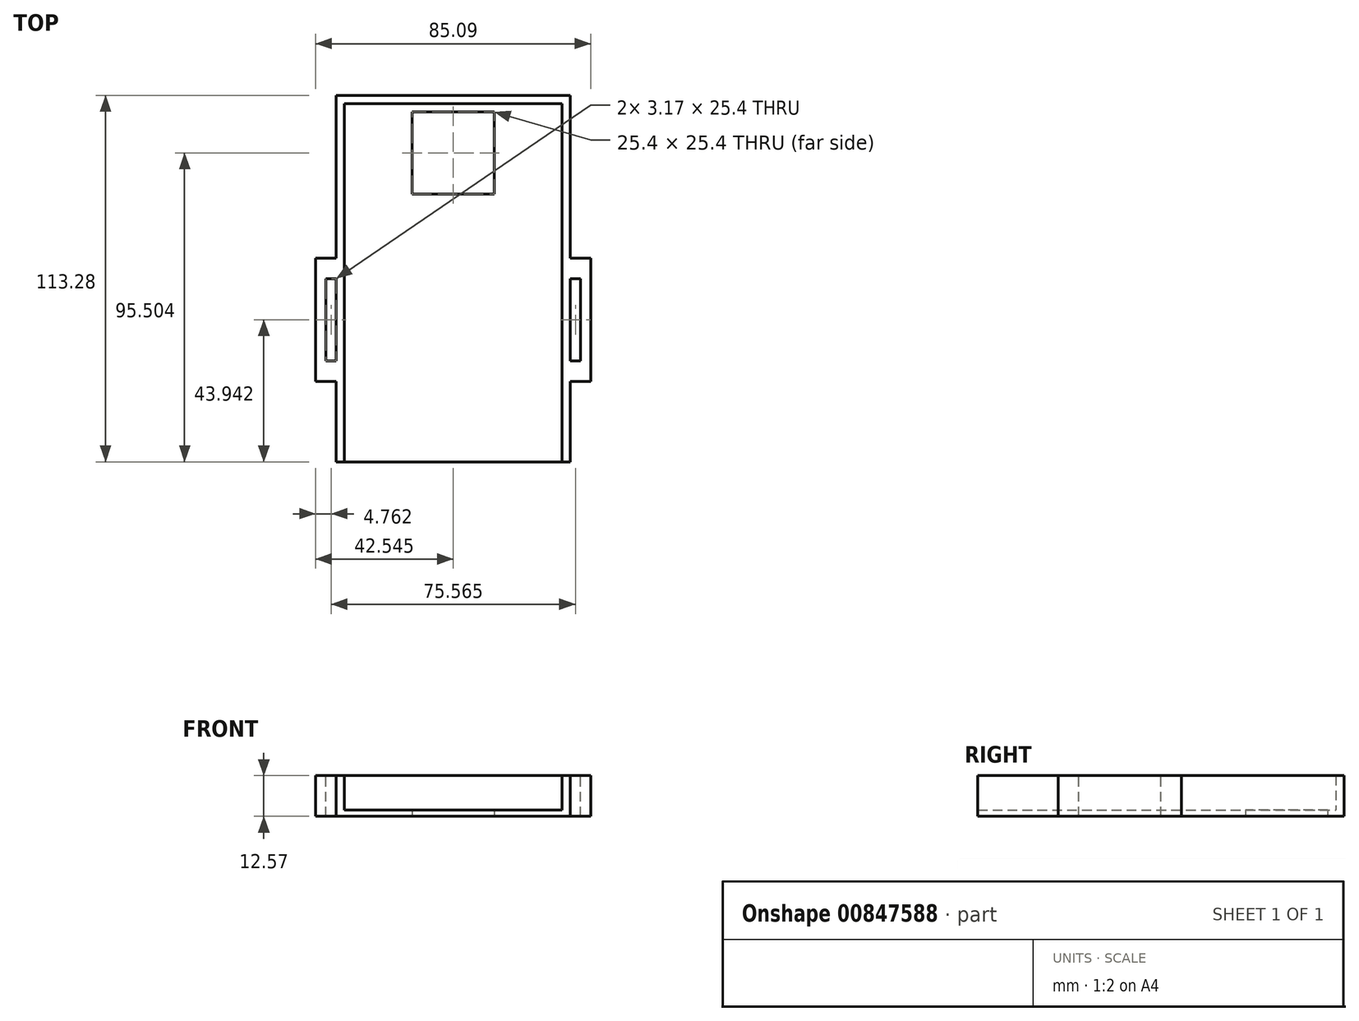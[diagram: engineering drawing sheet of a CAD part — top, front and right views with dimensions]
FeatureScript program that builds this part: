
annotation { "Feature Type Name" : "Feature", "Feature Type Description" : "" }
export const myFeature = defineFeature(function(context is Context, id is Id, definition is map)
    precondition{}
    {
        {
            var Q0;
            Q0=qCreatedBy(makeId("Top.planeOp"),FACE);
            var sketch = newSketch(context, id + "F0", { "sketchPlane" : qUnion([Q0])});
            skLineSegment(sketch, "E0.bottom", {"start": v(0, 0) * mm, "end": v(72.39, 0) * mm});
            skLineSegment(sketch, "E0.top", {"start": v(0, 138.68) * mm, "end": v(72.39, 138.68) * mm});
            skLineSegment(sketch, "E0.left", {"start": v(0, 0) * mm, "end": v(0, 138.68) * mm});
            skLineSegment(sketch, "E0.right", {"start": v(72.39, 0) * mm, "end": v(72.39, 138.68) * mm});
            skSolve(sketch);
        }
        {
            var Q0;
            Q0 = qSketchRegion(id + "F0", true);
            extrude(context, id + "F1", {"entities" : qUnion([Q0]), "depth" : 1.9 * mm, "offsetDistance" : 25.4 * mm});
        }
        {
            var Q0;
            Q0=makeQuery(id+"F1.opExtrude","CAP_FACE",FACE,{"disambiguationData":[OSD([sQuery(id+"F0.wireOp",EDGE,"E0.bottom"),sQuery(id+"F0.wireOp",EDGE,"E0.top"),sQuery(id+"F0.wireOp",EDGE,"E0.left"),sQuery(id+"F0.wireOp",EDGE,"E0.right")])],"isStart":false});
            var sketch = newSketch(context, id + "F2", { "sketchPlane" : qUnion([Q0])});
            skLineSegment(sketch, "E1.bottom", {"start": v(0, 0) * mm, "end": v(72.39, 0) * mm});
            skLineSegment(sketch, "E1.top", {"start": v(0, 138.68) * mm, "end": v(72.39, 138.68) * mm});
            skLineSegment(sketch, "E1.left", {"start": v(0, 0) * mm, "end": v(0, 138.68) * mm});
            skLineSegment(sketch, "E1.right", {"start": v(72.39, 0) * mm, "end": v(72.39, 138.68) * mm});
            skLineSegment(sketch, "E2.bottom", {"start": v(2.54, 2.54) * mm, "end": v(69.85, 2.54) * mm});
            skLineSegment(sketch, "E2.top", {"start": v(2.54, 136.14) * mm, "end": v(69.85, 136.14) * mm});
            skLineSegment(sketch, "E2.left", {"start": v(2.54, 2.54) * mm, "end": v(2.54, 136.14) * mm});
            skLineSegment(sketch, "E2.right", {"start": v(69.85, 2.54) * mm, "end": v(69.85, 136.14) * mm});
            skSolve(sketch);
        }
        {
            var Q0;
            Q0 = qSketchRegion(id + "F2", true);
            extrude(context, id + "F3", {"entities" : qUnion([Q0]), "operationType" : NewBodyOperationType.ADD, "depth" : 10.67 * mm, "offsetDistance" : 25.4 * mm});
        }
        {
            var Q0;
            Q0=makeQuery(id+"F1.opExtrude","CAP_FACE",FACE,{"disambiguationData":[OSD([sQuery(id+"F0.wireOp",EDGE,"E0.bottom"),sQuery(id+"F0.wireOp",EDGE,"E0.top"),sQuery(id+"F0.wireOp",EDGE,"E0.left"),sQuery(id+"F0.wireOp",EDGE,"E0.right")])],"isStart":true});
            var sketch = newSketch(context, id + "F4", { "sketchPlane" : qUnion([Q0])});
            skLineSegment(sketch, "E3.bottom", {"start": v(48.9, -133.6) * mm, "end": v(23.5, -133.6) * mm});
            skLineSegment(sketch, "E3.top", {"start": v(48.9, -108.2) * mm, "end": v(23.5, -108.2) * mm});
            skLineSegment(sketch, "E3.left", {"start": v(48.9, -133.6) * mm, "end": v(48.9, -108.2) * mm});
            skLineSegment(sketch, "E3.right", {"start": v(23.5, -133.6) * mm, "end": v(23.5, -108.2) * mm});
            skSolve(sketch);
        }
        {
            var Q0;
            Q0 = qSketchRegion(id + "F4", true);
            extrude(context, id + "F5", {"entities" : qUnion([Q0]), "operationType" : NewBodyOperationType.REMOVE, "endBound" : BoundingType.UP_TO_NEXT, "oppositeDirection" : true, "depth" : 25.4 * mm, "offsetDistance" : 25.4 * mm});
        }
        {
            var Q0;
            Q0=makeQuery(id+"F3.boolean.opBoolean","MERGE",FACE,{"derivedFrom":[makeQuery(id+"F1.opExtrude","SWEPT_FACE",FACE,{"disambiguationData":[OSD([sQuery(id+"F0.wireOp",EDGE,"E0.right")])]}),makeQuery(id+"F3.opExtrude","SWEPT_FACE",FACE,{"disambiguationData":[OSD([sQuery(id+"F2.wireOp",EDGE,"E1.right")])]})]});
            var sketch = newSketch(context, id + "F6", { "sketchPlane" : qUnion([Q0])});
            skLineSegment(sketch, "E4.left", {"start": v(56.64, 0) * mm, "end": v(56.64, 12.57) * mm});
            skLineSegment(sketch, "E4.right", {"start": v(82.04, 0) * mm, "end": v(82.04, 12.57) * mm});
            skLineSegment(sketch, "E5.bottom", {"start": v(56.64, 12.57) * mm, "end": v(50.3, 12.57) * mm});
            skLineSegment(sketch, "E5.top", {"start": v(56.64, 0) * mm, "end": v(50.3, 0) * mm});
            skLineSegment(sketch, "E5.left", {"start": v(56.64, 12.57) * mm, "end": v(56.64, 0) * mm});
            skLineSegment(sketch, "E5.right", {"start": v(50.3, 12.57) * mm, "end": v(50.3, 0) * mm});
            skLineSegment(sketch, "E6.bottom", {"start": v(82.04, 12.57) * mm, "end": v(88.4, 12.57) * mm});
            skLineSegment(sketch, "E6.top", {"start": v(82.04, 0) * mm, "end": v(88.4, 0) * mm});
            skLineSegment(sketch, "E6.left", {"start": v(82.04, 12.57) * mm, "end": v(82.04, 0) * mm});
            skLineSegment(sketch, "E6.right", {"start": v(88.4, 12.57) * mm, "end": v(88.4, 0) * mm});
            skSolve(sketch);
        }
        {
            var Q0;
            Q0 = qSketchRegion(id + "F6", true);
            extrude(context, id + "F7", {"entities" : qUnion([Q0]), "operationType" : NewBodyOperationType.ADD, "depth" : 3.17 * mm, "offsetDistance" : 25.4 * mm});
        }
        {
            var Q0;
            Q0=makeQuery(id+"F7.opExtrude","SWEPT_FACE",FACE,{"disambiguationData":[OSD([sQuery(id+"F6.wireOp",EDGE,"E5.right")])]});
            var sketch = newSketch(context, id + "F8", { "sketchPlane" : qUnion([Q0])});
            skLineSegment(sketch, "E7.bottom", {"start": v(75.56, 0) * mm, "end": v(78.74, 0) * mm});
            skLineSegment(sketch, "E7.top", {"start": v(75.56, 12.57) * mm, "end": v(78.74, 12.57) * mm});
            skLineSegment(sketch, "E7.left", {"start": v(75.56, 0) * mm, "end": v(75.56, 12.57) * mm});
            skLineSegment(sketch, "E7.right", {"start": v(78.74, 0) * mm, "end": v(78.74, 12.57) * mm});
            skSolve(sketch);
        }
        {
            var Q0;
            Q0 = qSketchRegion(id + "F8", true);
            var Q1;
            Q1=makeQuery(id+"F7.opExtrude","SWEPT_FACE",FACE,{"disambiguationData":[OSD([sQuery(id+"F6.wireOp",EDGE,"E6.right")])]});
            extrude(context, id + "F9", {"entities" : qUnion([Q0]), "operationType" : NewBodyOperationType.ADD, "endBound" : BoundingType.UP_TO_SURFACE, "oppositeDirection" : true, "depth" : 25.4 * mm, "endBoundEntityFace" : qUnion([Q1]), "offsetDistance" : 25.4 * mm});
        }
        {
            var Q0;
            Q0=makeQuery(id+"F9.boolean.opBoolean","MERGE",FACE,{"derivedFrom":[makeQuery(id+"F7.boolean.opBoolean","MERGE",FACE,{"derivedFrom":[makeQuery(id+"F3.opExtrude","CAP_FACE",FACE,{"disambiguationData":[OSD([sQuery(id+"F2.wireOp",EDGE,"E1.bottom"),sQuery(id+"F2.wireOp",EDGE,"E1.top"),sQuery(id+"F2.wireOp",EDGE,"E1.left"),sQuery(id+"F2.wireOp",EDGE,"E1.right"),sQuery(id+"F2.wireOp",EDGE,"E2.bottom"),sQuery(id+"F2.wireOp",EDGE,"E2.top"),sQuery(id+"F2.wireOp",EDGE,"E2.left"),sQuery(id+"F2.wireOp",EDGE,"E2.right")])],"isStart":false}),makeQuery(id+"F7.opExtrude","SWEPT_FACE",FACE,{"disambiguationData":[OSD([sQuery(id+"F6.wireOp",EDGE,"E5.bottom")])]}),makeQuery(id+"F7.opExtrude","SWEPT_FACE",FACE,{"disambiguationData":[OSD([sQuery(id+"F6.wireOp",EDGE,"E6.bottom")])]})]}),makeQuery(id+"F9.opExtrude","SWEPT_FACE",FACE,{"disambiguationData":[OSD([sQuery(id+"F8.wireOp",EDGE,"E7.top")])]})]});
            var sketch = newSketch(context, id + "F10", { "sketchPlane" : qUnion([Q0])});
            skLineSegment(sketch, "E8.bottom", {"start": v(0, 88.4) * mm, "end": v(-6.35, 88.4) * mm});
            skLineSegment(sketch, "E8.top", {"start": v(0, 82.04) * mm, "end": v(-6.35, 82.04) * mm});
            skLineSegment(sketch, "E8.left", {"start": v(0, 88.4) * mm, "end": v(0, 82.04) * mm});
            skLineSegment(sketch, "E8.right", {"start": v(-6.35, 88.4) * mm, "end": v(-6.35, 82.04) * mm});
            skLineSegment(sketch, "E9.bottom", {"start": v(-6.35, 50.3) * mm, "end": v(0, 50.3) * mm});
            skLineSegment(sketch, "E9.top", {"start": v(-6.35, 56.64) * mm, "end": v(0, 56.64) * mm});
            skLineSegment(sketch, "E9.left", {"start": v(-6.35, 50.3) * mm, "end": v(-6.35, 56.64) * mm});
            skLineSegment(sketch, "E9.right", {"start": v(0, 50.3) * mm, "end": v(0, 56.64) * mm});
            skLineSegment(sketch, "E10.bottom", {"start": v(-6.35, 56.64) * mm, "end": v(-3.18, 56.64) * mm});
            skLineSegment(sketch, "E10.top", {"start": v(-6.35, 82.04) * mm, "end": v(-3.18, 82.04) * mm});
            skLineSegment(sketch, "E10.left", {"start": v(-6.35, 56.64) * mm, "end": v(-6.35, 82.04) * mm});
            skLineSegment(sketch, "E10.right", {"start": v(-3.18, 56.64) * mm, "end": v(-3.18, 82.04) * mm});
            skSolve(sketch);
        }
        {
            var Q0;
            Q0 = qSketchRegion(id + "F10", true);
            var Q1;
            Q1=makeQuery(id+"F9.boolean.opBoolean","MERGE",FACE,{"derivedFrom":[makeQuery(id+"F7.boolean.opBoolean","MERGE",FACE,{"derivedFrom":[makeQuery(id+"F1.opExtrude","CAP_FACE",FACE,{"disambiguationData":[OSD([sQuery(id+"F0.wireOp",EDGE,"E0.bottom"),sQuery(id+"F0.wireOp",EDGE,"E0.top"),sQuery(id+"F0.wireOp",EDGE,"E0.left"),sQuery(id+"F0.wireOp",EDGE,"E0.right")])],"isStart":true}),makeQuery(id+"F7.opExtrude","SWEPT_FACE",FACE,{"disambiguationData":[OSD([sQuery(id+"F6.wireOp",EDGE,"E5.top")])]}),makeQuery(id+"F7.opExtrude","SWEPT_FACE",FACE,{"disambiguationData":[OSD([sQuery(id+"F6.wireOp",EDGE,"E6.top")])]})]}),makeQuery(id+"F9.opExtrude","SWEPT_FACE",FACE,{"disambiguationData":[OSD([sQuery(id+"F8.wireOp",EDGE,"E7.bottom")])]})]});
            extrude(context, id + "F11", {"entities" : qUnion([Q0]), "operationType" : NewBodyOperationType.ADD, "endBound" : BoundingType.UP_TO_SURFACE, "oppositeDirection" : true, "depth" : 25.4 * mm, "endBoundEntityFace" : qUnion([Q1]), "offsetDistance" : 25.4 * mm});
        }
        {
            var Q0;
            {var subQ0=sQuery(id+"F8.wireOp",EDGE,"E7.bottom");var subQ1=sQuery(id+"F6.wireOp",EDGE,"E6.top");var subQ2=sQuery(id+"F6.wireOp",EDGE,"E5.top");var subQ3=sQuery(id+"F0.wireOp",EDGE,"E0.right");var subQ4=sQuery(id+"F0.wireOp",EDGE,"E0.left");var subQ5=sQuery(id+"F0.wireOp",EDGE,"E0.top");var subQ6=sQuery(id+"F0.wireOp",EDGE,"E0.bottom");Q0=makeQuery(id+"F11.boolean.opBoolean","MERGE",FACE,{"derivedFrom":[makeQuery(id+"F9.boolean.opBoolean","MERGE",FACE,{"derivedFrom":[makeQuery(id+"F7.boolean.opBoolean","MERGE",FACE,{"derivedFrom":[makeQuery(id+"F1.opExtrude","CAP_FACE",FACE,{"disambiguationData":[OSD([subQ6,subQ5,subQ4,subQ3])],"isStart":true}),makeQuery(id+"F7.opExtrude","SWEPT_FACE",FACE,{"disambiguationData":[OSD([subQ2])]}),makeQuery(id+"F7.opExtrude","SWEPT_FACE",FACE,{"disambiguationData":[OSD([subQ1])]})]}),makeQuery(id+"F9.opExtrude","SWEPT_FACE",FACE,{"disambiguationData":[OSD([subQ0])]})]}),makeQuery(id+"F11.opExtrude","CAP_FACE",FACE,{"disambiguationData":[OSD([subQ6,subQ5,subQ4,subQ3,subQ2,subQ1,subQ0])],"isStart":false})]});}
            var sketch = newSketch(context, id + "F12", { "sketchPlane" : qUnion([Q0])});
            skLineSegment(sketch, "E11.bottom", {"start": v(72.39, 0) * mm, "end": v(0, 0) * mm});
            skLineSegment(sketch, "E11.top", {"start": v(72.39, -25.4) * mm, "end": v(0, -25.4) * mm});
            skLineSegment(sketch, "E11.left", {"start": v(72.39, 0) * mm, "end": v(72.39, -25.4) * mm});
            skLineSegment(sketch, "E11.right", {"start": v(0, 0) * mm, "end": v(0, -25.4) * mm});
            skSolve(sketch);
        }
        {
            var Q0;
            Q0=makeQuery(id+"F12.imprint","IMPRINT",FACE,{"disambiguationData":[TD([[makeQuery(id+"F12.imprint","IMPRINT",EDGE,{"derivedFrom":sQuery(id+"F12.wireOp",EDGE,"E11.bottom")}),-1.0]])]});
            extrude(context, id + "F13", {"entities" : qUnion([Q0]), "operationType" : NewBodyOperationType.REMOVE, "endBound" : BoundingType.THROUGH_ALL, "oppositeDirection" : true, "depth" : 25.4 * mm, "offsetDistance" : 25.4 * mm});
        }
    });
